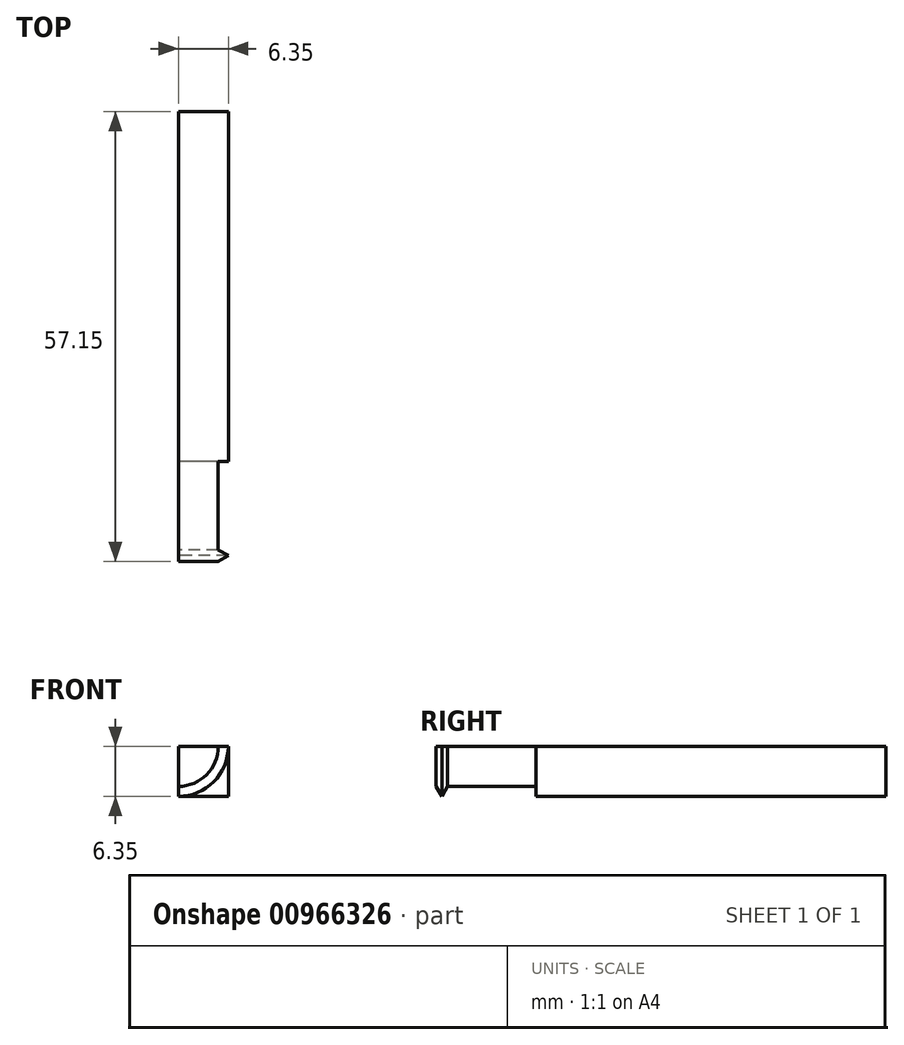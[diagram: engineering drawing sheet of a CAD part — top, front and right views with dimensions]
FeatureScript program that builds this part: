
annotation { "Feature Type Name" : "Feature", "Feature Type Description" : "" }
export const myFeature = defineFeature(function(context is Context, id is Id, definition is map)
    precondition{}
    {
        {
            var Q0;
            Q0=qCreatedBy(makeId("Front.planeOp"),FACE);
            var sketch = newSketch(context, id + "F0", { "sketchPlane" : qUnion([Q0])});
            skLineSegment(sketch, "E0.bottom", {"start": v(0, 0) * mm, "end": v(-6.35, 0) * mm});
            skLineSegment(sketch, "E0.top", {"start": v(0, -6.35) * mm, "end": v(-6.35, -6.35) * mm});
            skLineSegment(sketch, "E0.left", {"start": v(0, 0) * mm, "end": v(0, -6.35) * mm});
            skLineSegment(sketch, "E0.right", {"start": v(-6.35, 0) * mm, "end": v(-6.35, -6.35) * mm});
            skPoint(sketch, "E0.middle", {"position": v(0, 0) * mm});
            skSolve(sketch);
        }
        {
            var Q0;
            Q0=qSketchRegion(id+"F0",true);
            extrude(context, id + "F1", {"entities" : qUnion([Q0]), "depth" : 0 * mm, "offsetDistance" : 25.4 * mm, "hasSecondDirection" : true, "secondDirectionOppositeDirection" : true, "secondDirectionDepth" : 57.15 * mm});
        }
        {
            var Q0;
            Q0=qCreatedBy(makeId("Top.planeOp"),FACE);
            var sketch = newSketch(context, id + "F2", { "sketchPlane" : qUnion([Q0])});
            skLineSegment(sketch, "E1", {"start": v(-1.27, 0) * mm, "end": v(0, 0.73) * mm});
            skLineSegment(sketch, "E2", {"start": v(0, 0.73) * mm, "end": v(-1.27, 1.47) * mm});
            skLineSegment(sketch, "E3", {"start": v(-1.27, 1.47) * mm, "end": v(-1.27, 12.7) * mm});
            skLineSegment(sketch, "E4", {"start": v(-1.27, 12.7) * mm, "end": v(5.08, 12.7) * mm});
            skLineSegment(sketch, "E5", {"start": v(5.08, 12.7) * mm, "end": v(5.08, -1.27) * mm});
            skLineSegment(sketch, "E6", {"start": v(5.08, -1.27) * mm, "end": v(-1.27, -1.27) * mm});
            skLineSegment(sketch, "E7", {"start": v(-1.27, -1.27) * mm, "end": v(-1.27, 0) * mm});
            skLineSegment(sketch, "E8", {"start": v(-6.35, -5) * mm, "end": v(-6.35, 17.65) * mm, "construction": true});
            skSolve(sketch);
        }
        {
            var Q0;
            Q0 = qSketchRegion(id + "F2", true);
            var Q1;
            Q1=sQuery(id+"F2.wireOp",EDGE,"E8");
            revolve(context, id + "F3", {"operationType" : NewBodyOperationType.REMOVE, "surfaceOperationType" : NewSurfaceOperationType.NEW, "entities" : qUnion([Q0]), "axis" : qUnion([Q1]), "revolveType" : RevolveType.FULL, "oppositeDirection" : true});
        }
    });
